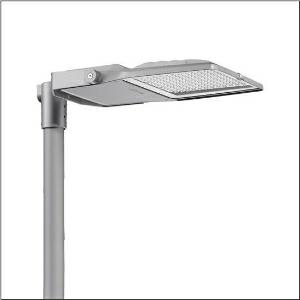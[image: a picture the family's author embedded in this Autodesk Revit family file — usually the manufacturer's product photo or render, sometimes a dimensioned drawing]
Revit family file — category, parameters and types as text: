
# Revit family: floodlight_fl_21_iq_midi___pl64_5xa7781f2e3a_9caf
name_source: partatom
category: Lighting Fixtures
units: mm (PartAtom-declared; Revit-internal decimal feet)

## family parameters
Cut with Voids When Loaded = No
Host = Face
Light Source = No
Part Type = Normal
Room Calculation Point = No
Round Connector Dimension = Use Diameter
Shared = No

## types (1)
- --- (1 x LED, 34530 lm, 270.2 W, 3000K)
    Apparent Load = 270 VA
    CIE Flux Codes = 28 80 98 100 100
    Color Rendering = 70
    Color Temperature = 3000K
    Default Elevation = 1800 mm
    Description = Floodlight FL 21 iQ midi, floodlight, primary light control with lens, of PMMA, primary optical cover: protective disc, of toughened safety glass, transparent, light distribution: PL64, light emission: direct distribution, installation type: surface-mounted, LED, High Power LED, rated luminous flux: 34.530lm, luminous efficacy: 128lm/W, light colour: 730, colour temperature: 3000K, control gear: iQ Comfort/DALI, control: optimised constant luminous flux control (CLO 2.0), Desk-Remote (wireless, voltage-free reading and setting of iQ features in the workshop via application-optimized NFC function/RFID function), Light-Fading, Smart-Wire, Night-Set, Lumen-Switch, Temp-Guard, Auto-Match, with terminal, 6-pole, mains connection: 220..240V, AC, 50/60Hz, start of lifetime: 270W, end of service life: 287W, reduction: 117W, luminaire housing, of diecast aluminium, powder-coated, Siteco® metallic grey (DB 702S), corrosivity category C5 mid according to DIN EN ISO 12944, suitable for swimming pools, chlorine-resistant, sealing non-destructively replaceable, please order mast flange separately, mast bracket, of steel, galvanised, powder-coated, Siteco® metallic grey (DB 702S), protection rating (complete): IP66, insulation class (complete): insulation class II (safety insulation), certification: CE, ENEC, VDE, protection symbol: D, impact resistance: IK08, permissible operating ambient temperature: -40..+40°C, permissible operating ambient temperature for outdoor applications: -40..+50°C, standard: DIN EN 12944, LABS conformity tested according to VDMA 24364:2018-05, packaging unit: 1 piece

Light Distribution: PL64
    Height = 76 mm
    Lamp = 1 x LED
    Lamp Light Flux = 34530 lm
    Lamp Power = 270.2 W
    Lamp count = 1
    Length = 657 mm
    Luminous efficacy = 128 lm/W
    Manufacturer = Siteco
    ModVariant = No
    Model = 5XA7781F2E3A
    Number of Poles = 1
    OnlyDefault = Yes
    Power Factor = 1
    Product Name = Floodlight FL 21 iQ midi | PL64
    Product group = floodlight | pylon annexe
    ProductGroupID = 6200
    Protection Class = Protection class II
    Protection Degree = IP 66
    RLX_Detail_Level = 1
    RLX_Emergency_Light_Flux = 0 lm
    RLX_Emergency_Type = 0
    RLX_Emergency_Type_DB = No
    RlxData = <blob elided: 153729 chars, md5=98f2b13e>
    Socket = socket
    Standby Power = 0 W
    System Light Flux = 34530 lm
    System Power = 270 W
    Type Comments = factory setting: luminous flux: 100 % | dim-lin: 254 | 620 mA
    Type Image = l_1007123.jpg
    URL = http://relux.com
    VarID = @adj_106868
    Voltage = 0 V
    Weight = 0.00 kg
    Width = 442 mm

## geometry (parser evidence)
native form markers: Blend x4, Sweep x11
no freeform markers — native parametric forms only
